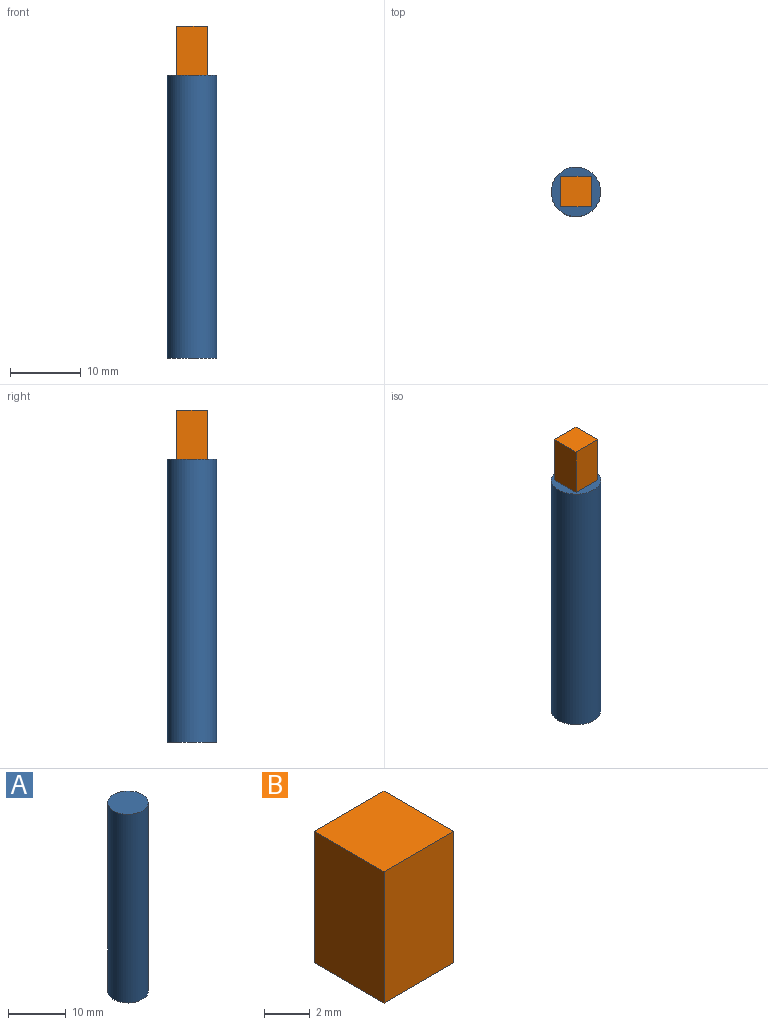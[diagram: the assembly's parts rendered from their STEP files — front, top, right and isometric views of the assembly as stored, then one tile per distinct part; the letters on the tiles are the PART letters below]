
ASSEMBLY  parts=2 mates=1
PART A: 3 faces, bbox 7x7x40 mm
  f0: cylinder r=3.5mm len=40mm, axis (0,0,-1), area 879.6mm2, adj f1,f2
  f1: plane 7x7mm, normal (0,0,1), area 38.5mm2, adj f0
  f2: plane 7x7mm, normal (0,0,-1), area 38.5mm2, adj f0
PART B: 6 faces, bbox 4.3x4.3x7 mm
  f0: plane 7x4.3mm, normal (0,-1,0), area 30.1mm2, adj f1,f3,f4,f5
  f1: plane 7x4.3mm, normal (1,0,0), area 30.1mm2, adj f0,f2,f4,f5
  f2: plane 7x4.3mm, normal (0,1,0), area 30.1mm2, adj f1,f3,f4,f5
  f3: plane 7x4.3mm, normal (-1,0,0), area 30.1mm2, adj f0,f2,f4,f5
  f4: plane 4.3x4.3mm, normal (0,0,1), area 18.5mm2, adj f0,f1,f2,f3
  f5: plane 4.3x4.3mm, normal (0,0,-1), area 18.5mm2, adj f0,f1,f2,f3
PLACE A t=(-7.48,-0.92,-14.91)mm
PLACE B rot(axis=(1,0,0),180deg) t=(-7.48,-0.92,32.09)mm
MATE fastened B.f4 <-> A.f0  axis (0,0,-1) through (-7.48,-0.92,25.09)mm
